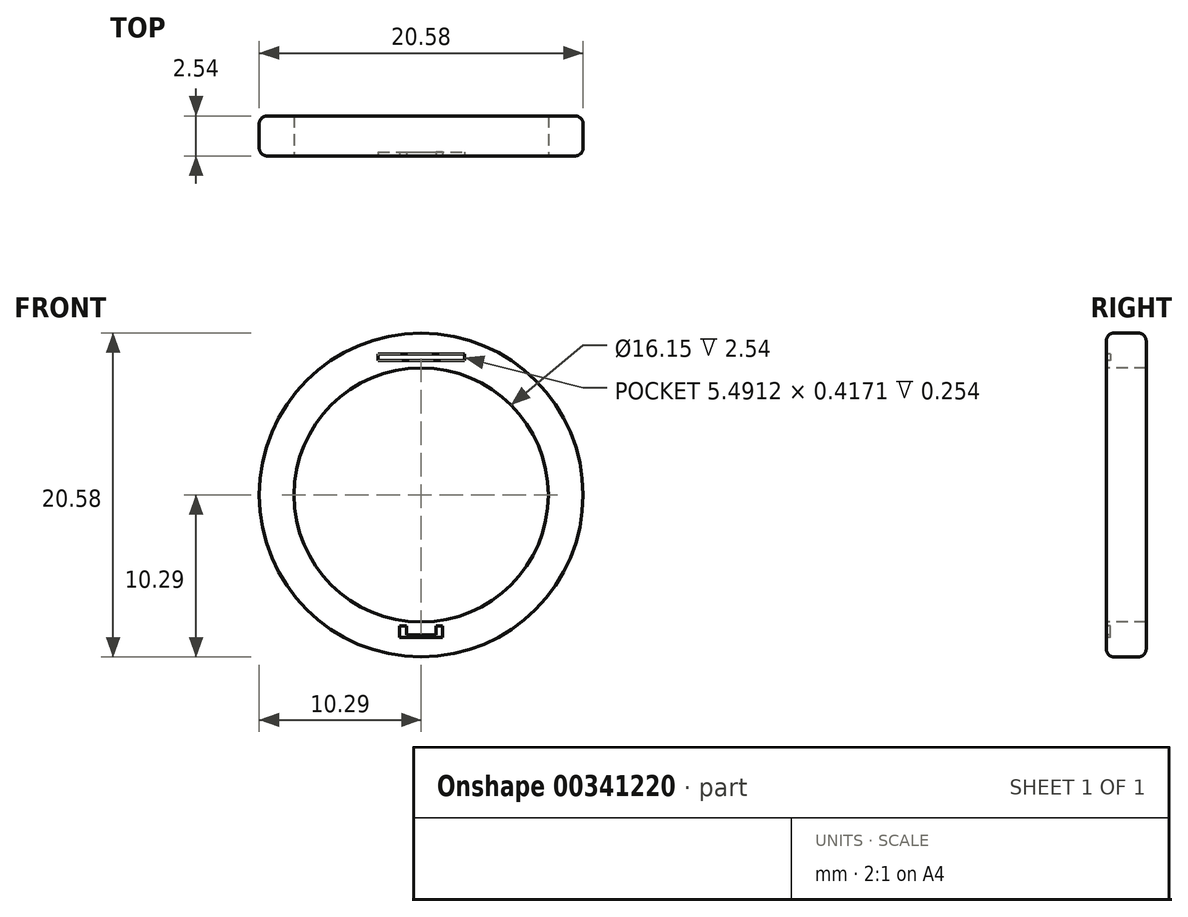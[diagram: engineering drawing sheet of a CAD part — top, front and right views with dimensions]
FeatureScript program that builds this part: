
annotation { "Feature Type Name" : "Feature", "Feature Type Description" : "" }
export const myFeature = defineFeature(function(context is Context, id is Id, definition is map)
    precondition{}
    {
        {
            var Q0;
            Q0=qCreatedBy(makeId("Front.planeOp"),FACE);
            var sketch = newSketch(context, id + "F0", { "sketchPlane" : qUnion([Q0])});
            skCircle(sketch, "E0", {"center": v(0, 0) * mm, "radius": 10.29 * mm});
            skCircle(sketch, "E1", {"center": v(0, 0) * mm, "radius": 8.07 * mm});
            skSolve(sketch);
        }
        {
            var Q0;
            Q0=makeQuery(id+"F0.imprint","IMPRINT",FACE,{"disambiguationData":[TD([[makeQuery(id+"F0.imprint","IMPRINT",EDGE,{"derivedFrom":sQuery(id+"F0.wireOp",EDGE,"E0")}),1.0]])]});
            extrude(context, id + "F1", {"entities" : qUnion([Q0]), "endBound" : BoundingType.SYMMETRIC, "oppositeDirection" : true, "depth" : 2.54 * mm});
        }
        {
            var Q0;
            Q0=makeQuery(id+"F1.opExtrude","CAP_EDGE",EDGE,{"disambiguationData":[OSD([sQuery(id+"F0.wireOp",EDGE,"E0")])],"isStart":true});
            fillet(context, id + "F2", {"entities" : qUnion([Q0]), "radius" : 0.5 * mm, "tangentPropagation" : true, "allowEdgeOverflow" : false});
        }
        {
            var Q0;
            Q0=makeQuery(id+"F1.opExtrude","CAP_EDGE",EDGE,{"disambiguationData":[OSD([sQuery(id+"F0.wireOp",EDGE,"E0")])],"isStart":false});
            fillet(context, id + "F3", {"entities" : qUnion([Q0]), "radius" : 0.5 * mm, "tangentPropagation" : true, "allowEdgeOverflow" : false});
        }
        {
            var Q0;
            Q0=makeQuery(id+"F1.opExtrude","CAP_FACE",FACE,{"disambiguationData":[OSD([sQuery(id+"F0.wireOp",EDGE,"E0"),sQuery(id+"F0.wireOp",EDGE,"E1")])],"isStart":true});
            var sketch = newSketch(context, id + "F4", { "sketchPlane" : qUnion([Q0])});
            skLineSegment(sketch, "E2.bottom", {"start": v(0, 8.95) * mm, "end": v(2.75, 8.95) * mm});
            skLineSegment(sketch, "E2.top", {"start": v(0, 8.53) * mm, "end": v(2.75, 8.53) * mm});
            skLineSegment(sketch, "E2.left", {"start": v(0, 8.95) * mm, "end": v(0, 8.53) * mm});
            skLineSegment(sketch, "E2.right", {"start": v(2.75, 8.95) * mm, "end": v(2.75, 8.53) * mm});
            skLineSegment(sketch, "E3.bottom", {"start": v(0, -9.05) * mm, "end": v(1.37, -9.05) * mm});
            skLineSegment(sketch, "E3.top", {"start": v(0, -8.88) * mm, "end": v(1.37, -8.88) * mm});
            skLineSegment(sketch, "E3.left", {"start": v(0, -9.05) * mm, "end": v(0, -8.88) * mm});
            skLineSegment(sketch, "E3.right", {"start": v(1.37, -9.05) * mm, "end": v(1.37, -8.88) * mm});
            skLineSegment(sketch, "E4.bottom", {"start": v(1.37, -8.88) * mm, "end": v(0.94, -8.88) * mm});
            skLineSegment(sketch, "E4.top", {"start": v(1.37, -8.32) * mm, "end": v(0.94, -8.32) * mm});
            skLineSegment(sketch, "E4.left", {"start": v(1.37, -8.88) * mm, "end": v(1.37, -8.32) * mm});
            skLineSegment(sketch, "E4.right", {"start": v(0.94, -8.88) * mm, "end": v(0.94, -8.32) * mm});
            skLineSegment(sketch, "E5.MirrorCS", {"start": v(0, 8.95) * mm, "end": v(-2.75, 8.95) * mm});
            skLineSegment(sketch, "E6.MirrorCS", {"start": v(0, 8.53) * mm, "end": v(-2.75, 8.53) * mm});
            skLineSegment(sketch, "E7.MirrorCS", {"start": v(-2.75, 8.95) * mm, "end": v(-2.75, 8.53) * mm});
            skLineSegment(sketch, "E8.MirrorCS", {"start": v(-0.94, -8.88) * mm, "end": v(-0.94, -8.32) * mm});
            skLineSegment(sketch, "E9.MirrorCS", {"start": v(-1.37, -8.88) * mm, "end": v(-1.37, -8.32) * mm});
            skLineSegment(sketch, "E10.MirrorCS", {"start": v(0, -8.88) * mm, "end": v(-1.37, -8.88) * mm});
            skLineSegment(sketch, "E11.MirrorCS", {"start": v(0, -9.05) * mm, "end": v(-1.37, -9.05) * mm});
            skLineSegment(sketch, "E12.MirrorCS", {"start": v(-1.37, -8.32) * mm, "end": v(-0.94, -8.32) * mm});
            skLineSegment(sketch, "E13.MirrorCS", {"start": v(-1.37, -9.05) * mm, "end": v(-1.37, -8.88) * mm});
            skSolve(sketch);
        }
        {
            var Q0;
            Q0 = qSketchRegion(id + "F4", true);
            extrude(context, id + "F5", {"entities" : qUnion([Q0]), "operationType" : NewBodyOperationType.REMOVE, "oppositeDirection" : true, "depth" : 0.25 * mm});
        }
    });
